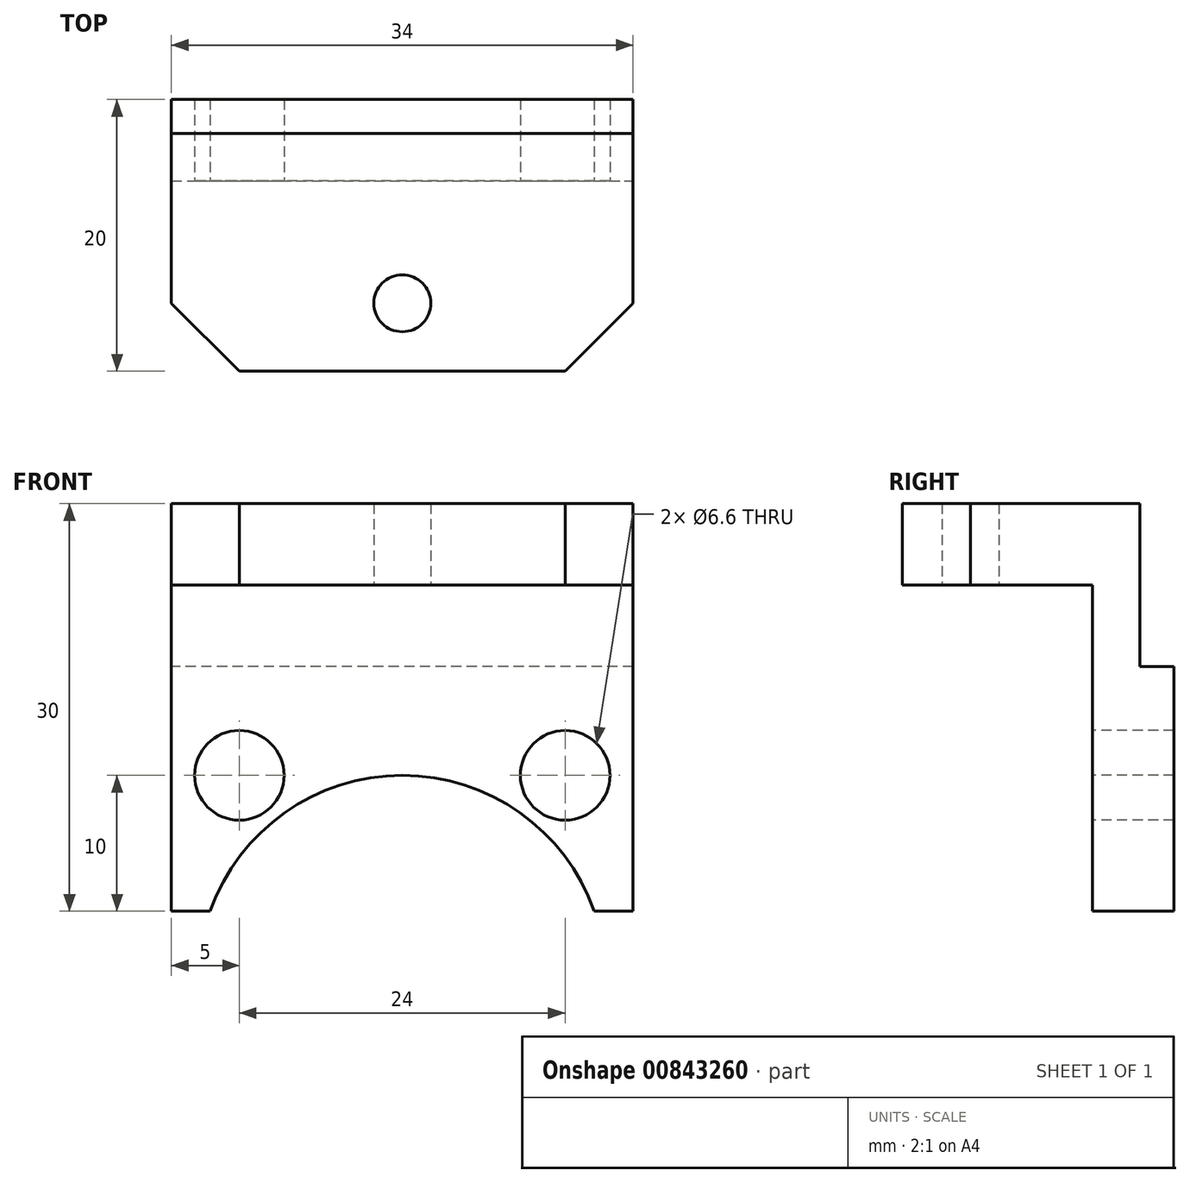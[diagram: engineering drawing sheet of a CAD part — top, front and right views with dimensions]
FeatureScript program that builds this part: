
annotation { "Feature Type Name" : "Feature", "Feature Type Description" : "" }
export const myFeature = defineFeature(function(context is Context, id is Id, definition is map)
    precondition{}
    {
        {
            var Q0;
            Q0=qCreatedBy(makeId("Front.planeOp"),FACE);
            var sketch = newSketch(context, id + "F0", { "sketchPlane" : qUnion([Q0])});
            skLineSegment(sketch, "E0.bottom", {"start": v(0, 0) * mm, "end": v(34, 0) * mm});
            skLineSegment(sketch, "E0.top", {"start": v(0, 30) * mm, "end": v(34, 30) * mm});
            skLineSegment(sketch, "E0.left", {"start": v(0, 0) * mm, "end": v(0, 30) * mm});
            skLineSegment(sketch, "E0.right", {"start": v(34, 0) * mm, "end": v(34, 30) * mm});
            skSolve(sketch);
        }
        {
            var Q0;
            Q0 = qSketchRegion(id + "F0", true);
            extrude(context, id + "F1", {"entities" : qUnion([Q0]), "depth" : 20 * mm, "offsetDistance" : 25 * mm});
        }
        {
            var Q0;
            Q0=makeQuery(id+"F1.opExtrude","CAP_FACE",FACE,{"disambiguationData":[OSD([sQuery(id+"F0.wireOp",EDGE,"E0.bottom"),sQuery(id+"F0.wireOp",EDGE,"E0.top"),sQuery(id+"F0.wireOp",EDGE,"E0.left"),sQuery(id+"F0.wireOp",EDGE,"E0.right")])],"isStart":false});
            var sketch = newSketch(context, id + "F2", { "sketchPlane" : qUnion([Q0])});
            skLineSegment(sketch, "E1", {"start": v(0, 24) * mm, "end": v(34, 24) * mm});
            skLineSegment(sketch, "E2", {"start": v(0, 24) * mm, "end": v(0, 0) * mm});
            skLineSegment(sketch, "E3", {"start": v(34, 0) * mm, "end": v(34, 24) * mm});
            skLineSegment(sketch, "E4", {"start": v(34, 0) * mm, "end": v(0, 0) * mm});
            skLineSegment(sketch, "E5", {"start": v(0, 0) * mm, "end": v(0, 24) * mm});
            skSolve(sketch);
        }
        {
            var Q0;
            Q0=makeQuery(id+"F2.imprint","IMPRINT",FACE,{"disambiguationData":[TD([[makeQuery(id+"F2.imprint","IMPRINT",EDGE,{"derivedFrom":sQuery(id+"F2.wireOp",EDGE,"E1")}),-1.0]])]});
            extrude(context, id + "F3", {"entities" : qUnion([Q0]), "operationType" : NewBodyOperationType.REMOVE, "oppositeDirection" : true, "depth" : 14 * mm, "offsetDistance" : 25 * mm});
        }
        {
            var Q0;
            Q0=makeQuery(id+"F3.boolean.opBoolean","COPY",FACE,{"derivedFrom":makeQuery(id+"F3.opExtrude","SWEPT_FACE",FACE,{"disambiguationData":[OSD([sQuery(id+"F2.wireOp",EDGE,"E1")])]})});
            var sketch = newSketch(context, id + "F4", { "sketchPlane" : qUnion([Q0])});
            skPoint(sketch, "E6", {"position": v(17, 15) * mm});
            skPoint(sketch, "E6.positionSnap0", {"position": v(17, 20) * mm});
            skPoint(sketch, "E7", {"position": v(34, 20) * mm});
            skSolve(sketch);
        }
        {
            var Q0;
            Q0=sQuery(id+"F4.wireOp",VERTEX,"E6");
            var Q1;
            Q1=makeQuery(id+"F1.opExtrude","SWEPT_BODY",BODY,{"disambiguationData":[OSD([sQuery(id+"F0.wireOp",EDGE,"E0.bottom"),sQuery(id+"F0.wireOp",EDGE,"E0.top"),sQuery(id+"F0.wireOp",EDGE,"E0.left"),sQuery(id+"F0.wireOp",EDGE,"E0.right")])]});
            hole(context, id + "F5", {"style" : HoleStyle.SIMPLE, "endStyle" : HoleEndStyle.BLIND, "standardTappedOrClearance" : lookupTablePath({ "standard" : "ISO", "engagement" : "75%", "pitch" : "0.8 mm", "size" : "M5", "type" : "Tapped" }), "standardBlindInLast" : lookupTablePath({ "standard" : "ISO", "engagement" : "75%", "pitch" : "0.8 mm", "size" : "M5", "type" : "Tapped" }), "holeDiameter" : 4.2 * mm, "majorDiameter" : 5 * mm, "showTappedDepth" : true, "holeDepth" : 20 * mm, "isTappedThrough" : true, "tappedDepth" : 17.6 * mm, "tapClearance" : 3, "locations" : qUnion([Q0]), "scope" : qUnion([Q1])});
        }
        {
            var Q0;
            Q0=makeQuery(id+"F1.opExtrude","CAP_EDGE",EDGE,{"disambiguationData":[OSD([sQuery(id+"F0.wireOp",EDGE,"E0.right")])],"isStart":false});
            var Q1;
            Q1=makeQuery(id+"F1.opExtrude","CAP_EDGE",EDGE,{"disambiguationData":[OSD([sQuery(id+"F0.wireOp",EDGE,"E0.left")])],"isStart":false});
            chamfer(context, id + "F6", {"entities" : qUnion([Q0, Q1]), "width" : 5 * mm, "tangentPropagation" : true});
        }
        {
            var Q0;
            Q0=makeQuery(id+"F3.boolean.opBoolean","COPY",FACE,{"derivedFrom":makeQuery(id+"F3.opExtrude","CAP_FACE",FACE,{"disambiguationData":[OSD([sQuery(id+"F2.wireOp",EDGE,"E1"),sQuery(id+"F2.wireOp",EDGE,"E3"),sQuery(id+"F2.wireOp",EDGE,"E4"),sQuery(id+"F2.wireOp",EDGE,"E5")])],"isStart":false})});
            var sketch = newSketch(context, id + "F7", { "sketchPlane" : qUnion([Q0])});
            skPoint(sketch, "E8", {"position": v(0, 12) * mm});
            skPoint(sketch, "E9", {"position": v(17, -5) * mm});
            skPoint(sketch, "E9.positionSnap0", {"position": v(17, 0) * mm});
            skPoint(sketch, "E10", {"position": v(5, 10) * mm});
            skPoint(sketch, "E11", {"position": v(29, 10) * mm});
            skCircle(sketch, "E12", {"center": v(17, -5) * mm, "radius": 15 * mm});
            skSolve(sketch);
        }
        {
            var Q0;
            {var subQ0=sQuery(id+"F7.wireOp",EDGE,"E12");var subQ1=makeQuery(id+"F3.boolean.opBoolean","COPY",EDGE,{"derivedFrom":makeQuery(id+"F3.opExtrude","CAP_EDGE",EDGE,{"disambiguationData":[OSD([sQuery(id+"F2.wireOp",EDGE,"E4")])],"isStart":false})});var subQ2=makeQuery(id+"F7.imprint","INTERSECT",VERTEX,{"disambiguationData":[OD(0.0)],"derivedFrom":[subQ1,subQ0]});Q0=makeQuery(id+"F7.imprint","IMPRINT",FACE,{"disambiguationData":[TD([[makeQuery(id+"F7.imprint","IMPRINT",EDGE,{"disambiguationData":[TD([[subQ2,1.0]])],"derivedFrom":subQ0}),1.0]])]});}
            var Q1;
            {var subQ0=sQuery(id+"F7.wireOp",EDGE,"E12");var subQ1=makeQuery(id+"F3.boolean.opBoolean","COPY",EDGE,{"derivedFrom":makeQuery(id+"F3.opExtrude","CAP_EDGE",EDGE,{"disambiguationData":[OSD([sQuery(id+"F2.wireOp",EDGE,"E4")])],"isStart":false})});var subQ2=makeQuery(id+"F7.imprint","INTERSECT",VERTEX,{"disambiguationData":[OD(0.0)],"derivedFrom":[subQ1,subQ0]});Q1=makeQuery(id+"F7.imprint","IMPRINT",FACE,{"disambiguationData":[TD([[makeQuery(id+"F7.imprint","IMPRINT",EDGE,{"disambiguationData":[TD([[subQ2,-1.0]])],"derivedFrom":subQ0}),1.0]])]});}
            extrude(context, id + "F8", {"entities" : qUnion([Q0, Q1]), "operationType" : NewBodyOperationType.REMOVE, "oppositeDirection" : true, "depth" : 25 * mm, "offsetDistance" : 25 * mm});
        }
        {
            var Q0;
            Q0=sQuery(id+"F7.wireOp",VERTEX,"E10");
            var Q1;
            Q1=sQuery(id+"F7.wireOp",VERTEX,"E11");
            var Q2;
            Q2=makeQuery(id+"F1.opExtrude","SWEPT_BODY",BODY,{"disambiguationData":[OSD([sQuery(id+"F0.wireOp",EDGE,"E0.bottom"),sQuery(id+"F0.wireOp",EDGE,"E0.top"),sQuery(id+"F0.wireOp",EDGE,"E0.left"),sQuery(id+"F0.wireOp",EDGE,"E0.right")])]});
            hole(context, id + "F9", {"style" : HoleStyle.SIMPLE, "endStyle" : HoleEndStyle.BLIND, "standardTappedOrClearance" : lookupTablePath({ "fit" : "Normal", "standard" : "ISO", "size" : "M6", "type" : "Clearance" }), "standardBlindInLast" : lookupTablePath({ "fit" : "Standard", "standard" : "ISO", "size" : "M6", "type" : "Clearance" }), "holeDiameter" : 6.6 * mm, "majorDiameter" : 5 * mm, "holeDepth" : 20 * mm, "isTappedThrough" : true, "tappedDepth" : 17.6 * mm, "tapClearance" : 3, "locations" : qUnion([Q0, Q1]), "scope" : qUnion([Q2])});
        }
        {
            var Q0;
            Q0=makeQuery(id+"F1.opExtrude","CAP_FACE",FACE,{"disambiguationData":[OSD([sQuery(id+"F0.wireOp",EDGE,"E0.bottom"),sQuery(id+"F0.wireOp",EDGE,"E0.top"),sQuery(id+"F0.wireOp",EDGE,"E0.left"),sQuery(id+"F0.wireOp",EDGE,"E0.right")])],"isStart":true});
            var sketch = newSketch(context, id + "F10", { "sketchPlane" : qUnion([Q0])});
            skLineSegment(sketch, "E13", {"start": v(-34, 18) * mm, "end": v(0, 18) * mm});
            skLineSegment(sketch, "E14", {"start": v(-34, 18) * mm, "end": v(-34, 30) * mm});
            skLineSegment(sketch, "E15", {"start": v(-34, 30) * mm, "end": v(0, 30) * mm});
            skLineSegment(sketch, "E16", {"start": v(0, 30) * mm, "end": v(0, 18) * mm});
            skSolve(sketch);
        }
        {
            var Q0;
            Q0=makeQuery(id+"F10.imprint","IMPRINT",FACE,{"disambiguationData":[TD([[makeQuery(id+"F10.imprint","IMPRINT",EDGE,{"derivedFrom":sQuery(id+"F10.wireOp",EDGE,"E13")}),1.0]])]});
            extrude(context, id + "F11", {"entities" : qUnion([Q0]), "operationType" : NewBodyOperationType.REMOVE, "oppositeDirection" : true, "depth" : 2.5 * mm, "offsetDistance" : 25 * mm});
        }
    });
